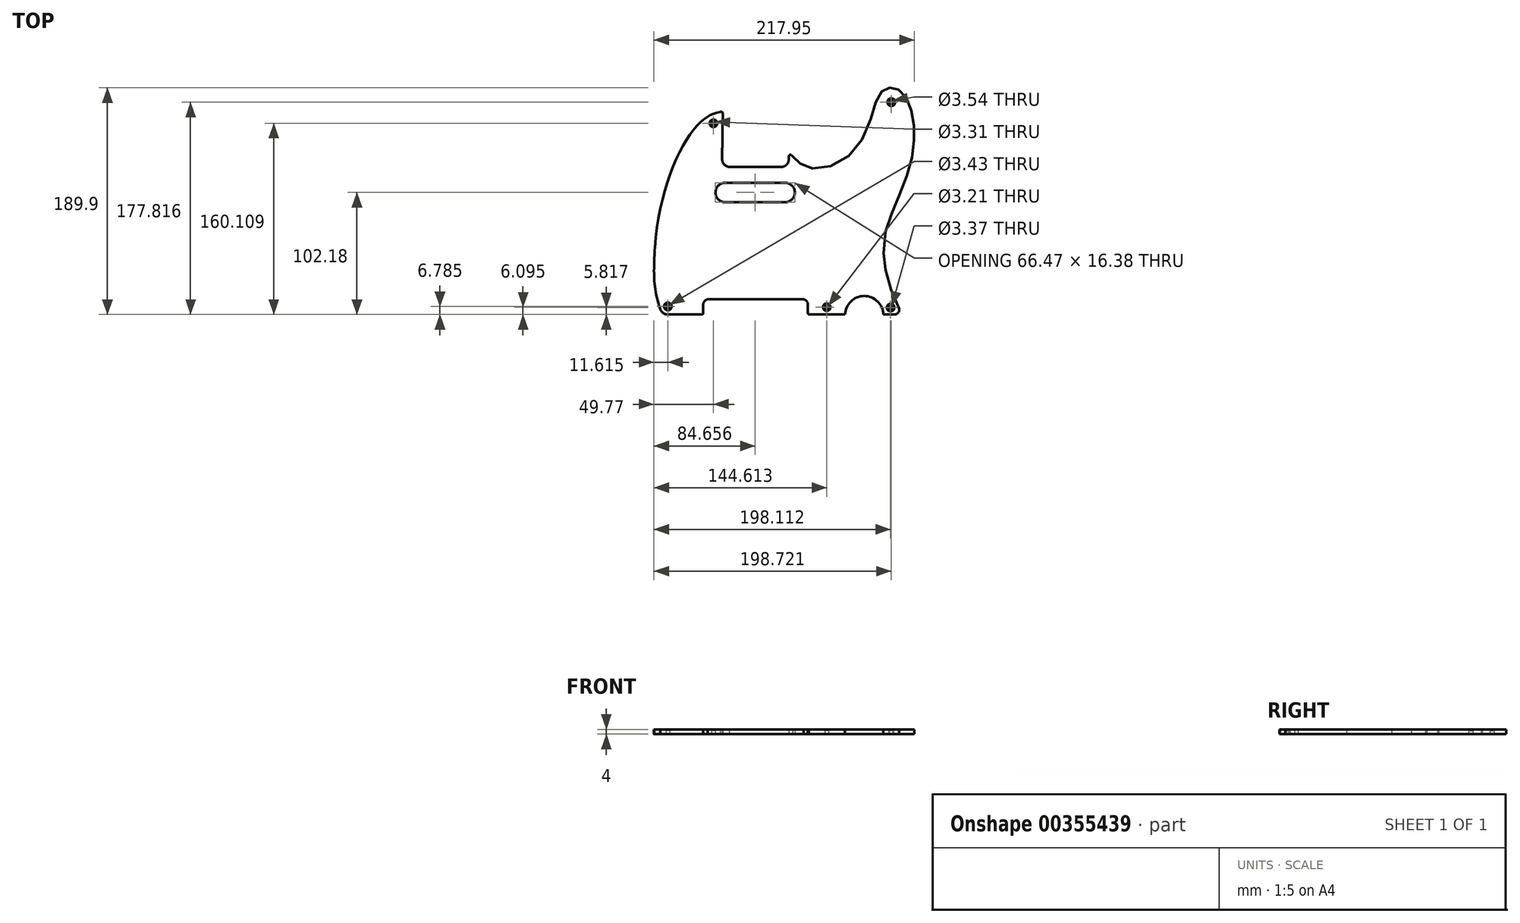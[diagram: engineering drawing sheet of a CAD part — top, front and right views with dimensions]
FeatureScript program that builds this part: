
annotation { "Feature Type Name" : "Feature", "Feature Type Description" : "" }
export const myFeature = defineFeature(function(context is Context, id is Id, definition is map)
    precondition{}
    {
        {
            var Q0;
            Q0=qCreatedBy(makeId("Top.planeOp"),FACE);
            var sketch = newSketch(context, id + "F0", { "sketchPlane" : qUnion([Q0])});
            skPoint(sketch, "E0.middle", {"position": v(0, 0) * mm});
            skCircle(sketch, "E1", {"center": v(-19.35, 182.39) * mm, "radius": 1.77 * mm});
            skCircle(sketch, "E2", {"center": v(-168.3, 164.68) * mm, "radius": 1.66 * mm});
            skLineSegment(sketch, "E3", {"start": v(-168.3, 164.68) * mm, "end": v(-19.35, 182.39) * mm, "construction": true});
            skCircle(sketch, "E4", {"center": v(-206.45, 11.36) * mm, "radius": 1.71 * mm});
            skCircle(sketch, "E5", {"center": v(-73.46, 10.66) * mm, "radius": 1.6 * mm});
            skCircle(sketch, "E6", {"center": v(-19.96, 10.39) * mm, "radius": 1.69 * mm});
            skLineSegment(sketch, "E7", {"start": v(-168.3, 164.68) * mm, "end": v(-206.45, 11.36) * mm, "construction": true});
            skLineSegment(sketch, "E8", {"start": v(-19.35, 182.39) * mm, "end": v(-19.96, 10.39) * mm, "construction": true});
            skLineSegment(sketch, "E9", {"start": v(-206.45, 11.36) * mm, "end": v(-73.46, 10.66) * mm, "construction": true});
            skLineSegment(sketch, "E10", {"start": v(-73.46, 10.66) * mm, "end": v(-19.96, 10.39) * mm, "construction": true});
            skLineSegment(sketch, "E11", {"start": v(-178.02, 4.57) * mm, "end": v(-206.45, 4.57) * mm});
            skArc(sketch, "E12", {"start": v(-206.45, 4.57) * mm, "mid": v(-210.44, 5.86) * mm, "end": v(-212.9, 9.25) * mm});
            skArc(sketch, "E13", {"start": v(-178.02, 4.57) * mm, "mid": v(-177.3, 4.81) * mm, "end": v(-176.88, 5.45) * mm});
            skLineSegment(sketch, "E14", {"start": v(-176.88, 5.45) * mm, "end": v(-176.88, 13.3) * mm});
            skArc(sketch, "E15", {"start": v(-173.21, 17.36) * mm, "mid": v(-175.63, 15.86) * mm, "end": v(-176.88, 13.3) * mm});
            skLineSegment(sketch, "E16", {"start": v(-173.21, 17.36) * mm, "end": v(-92.81, 17.36) * mm});
            skArc(sketch, "E17", {"start": v(-89.24, 13.4) * mm, "mid": v(-90.42, 15.92) * mm, "end": v(-92.81, 17.36) * mm});
            skLineSegment(sketch, "E18", {"start": v(-89.24, 13.4) * mm, "end": v(-89.24, 5.9) * mm});
            skArc(sketch, "E19", {"start": v(-89.24, 5.9) * mm, "mid": v(-89.04, 5.13) * mm, "end": v(-88.49, 4.57) * mm});
            skLineSegment(sketch, "E20", {"start": v(-88.49, 4.57) * mm, "end": v(-58.05, 4.57) * mm});
            skArc(sketch, "E21", {"start": v(-26.02, 4.57) * mm, "mid": v(-42.04, 20.07) * mm, "end": v(-58.05, 4.57) * mm});
            skLineSegment(sketch, "E22", {"start": v(-133.01, 17.36) * mm, "end": v(-133.01, -7.61) * mm});
            skLineSegment(sketch, "E23", {"start": v(-26.02, 4.57) * mm, "end": v(-16.76, 4.57) * mm});
            skArc(sketch, "E24", {"start": v(-16.76, 4.57) * mm, "mid": v(-13.6, 6.12) * mm, "end": v(-12.86, 9.57) * mm});
            skFitSpline(sketch, "E25", {"points": [v(-212.9, 9.25) * mm, v(-217.39, 60.66) * mm], "startDerivative": vector(-20.15, 57.1) * mm, "endDerivative": vector(2.26, 50.09) * mm});
            skFitSpline(sketch, "E26", {"points": [v(-217.39, 60.66) * mm, v(-183.96, 160.65) * mm, v(-162.78, 174.32) * mm], "startDerivative": vector(12.5, 194.87) * mm, "endDerivative": vector(62.55, 11.21) * mm});
            skLineSegment(sketch, "E27", {"start": v(-160.97, 134.38) * mm, "end": v(-160.56, 173.36) * mm});
            skFitSpline(sketch, "E28", {"points": [v(-162.78, 174.32) * mm, v(-161.45, 174.32) * mm, v(-160.56, 173.36) * mm], "startDerivative": vector(3.21, 0.26) * mm, "endDerivative": vector(1.04, -3.83) * mm});
            skArc(sketch, "E29", {"start": v(-160.97, 134.38) * mm, "mid": v(-159.24, 130.04) * mm, "end": v(-154.96, 128.16) * mm});
            skLineSegment(sketch, "E30", {"start": v(-154.96, 128.16) * mm, "end": v(-111.44, 128.16) * mm});
            skArc(sketch, "E31", {"start": v(-111.44, 128.16) * mm, "mid": v(-107.05, 129.99) * mm, "end": v(-105.26, 134.39) * mm});
            skLineSegment(sketch, "E32", {"start": v(-105.26, 137.04) * mm, "end": v(-105.26, 134.39) * mm});
            skFitSpline(sketch, "E33", {"points": [v(-105.26, 137.04) * mm, v(-101.96, 137.04) * mm], "startDerivative": vector(2.71, 7.99) * mm, "endDerivative": vector(1.53, -1.27) * mm});
            skFitSpline(sketch, "E34", {"points": [v(-12.86, 9.57) * mm, v(-17.7, 20.66) * mm, v(-22.68, 34.34) * mm, v(-24.82, 45.89) * mm, v(-25.82, 53.58) * mm, v(-25.08, 68.74) * mm, v(-22.74, 78.57) * mm, v(-18.85, 89.83) * mm, v(-13.4, 102.83) * mm, v(-8.78, 114.1) * mm, v(-4.77, 126.02) * mm, v(-2.07, 136.39) * mm, v(-0.63, 145.86) * mm, v(-0.12, 154.77) * mm, v(-0.37, 161.1) * mm, v(-1.1, 167.45) * mm, v(-2.5, 174.97) * mm, v(-3.72, 179.13) * mm, v(-6.29, 185.18) * mm, v(-9.27, 189.76) * mm, v(-11.97, 192.2) * mm, v(-15.18, 193.85) * mm, v(-17.8, 194.42) * mm, v(-19.67, 194.44) * mm, v(-22.19, 194.2) * mm, v(-23.88, 193.67) * mm, v(-26.53, 192.2) * mm, v(-28.77, 190) * mm, v(-31.45, 185.15) * mm, v(-33.5, 179.12) * mm, v(-36.18, 169.42) * mm, v(-41.23, 155.86) * mm, v(-49.68, 142.68) * mm, v(-58.8, 134.52) * mm, v(-71.85, 128.33) * mm, v(-82.35, 126.82) * mm, v(-89.76, 127.87) * mm, v(-94.34, 129.9) * mm, v(-97.85, 132.58) * mm, v(-100.24, 134.95) * mm, v(-101.96, 137.04) * mm, v(-102.75, 137.74) * mm], "startDerivative": vector(-150.29, 340.6) * mm, "endDerivative": vector(-84.46, 63.08) * mm});
            skLineSegment(sketch, "E35.bottom", {"start": v(-158.46, 98.56) * mm, "end": v(-108.37, 98.56) * mm});
            skLineSegment(sketch, "E35.top", {"start": v(-158.46, 114.94) * mm, "end": v(-108.37, 114.94) * mm});
            skLineSegment(sketch, "E35.left", {"start": v(-166.65, 106.75) * mm, "end": v(-166.65, 106.75) * mm});
            skLineSegment(sketch, "E35.right", {"start": v(-100.18, 106.75) * mm, "end": v(-100.18, 106.75) * mm});
            skPoint(sketch, "E36.visualSharp", {"position": v(-166.65, 114.94) * mm});
            skArc(sketch, "E36.filletArc", {"start": v(-158.46, 114.94) * mm, "mid": v(-164.25, 112.54) * mm, "end": v(-166.65, 106.75) * mm});
            skPoint(sketch, "E37.visualSharp", {"position": v(-166.65, 98.56) * mm});
            skArc(sketch, "E37.filletArc", {"start": v(-166.65, 106.75) * mm, "mid": v(-164.25, 100.96) * mm, "end": v(-158.46, 98.56) * mm});
            skPoint(sketch, "E38.visualSharp", {"position": v(-100.18, 114.94) * mm});
            skArc(sketch, "E38.filletArc", {"start": v(-100.18, 106.75) * mm, "mid": v(-102.58, 112.54) * mm, "end": v(-108.37, 114.94) * mm});
            skPoint(sketch, "E39.visualSharp", {"position": v(-100.18, 98.56) * mm});
            skArc(sketch, "E39.filletArc", {"start": v(-108.37, 98.56) * mm, "mid": v(-102.58, 100.96) * mm, "end": v(-100.18, 106.75) * mm});
            skSolve(sketch);
        }
        {
            var Q0;
            Q0=makeQuery(id+"F0.imprint","IMPRINT",FACE,{"disambiguationData":[TD([[makeQuery(id+"F0.imprint","IMPRINT",EDGE,{"derivedFrom":sQuery(id+"F0.wireOp",EDGE,"E1")}),-1.0]])]});
            extrude(context, id + "F1", {"entities" : qUnion([Q0]), "depth" : 4 * mm, "offsetDistance" : 25 * mm});
        }
        {
            var Q0;
            Q0=makeQuery(id+"F1.opExtrude","CAP_EDGE",EDGE,{"disambiguationData":[OSD([sQuery(id+"F0.wireOp",EDGE,"E2")])],"isStart":false});
            var Q1;
            Q1=makeQuery(id+"F1.opExtrude","CAP_EDGE",EDGE,{"disambiguationData":[OSD([sQuery(id+"F0.wireOp",EDGE,"E1")])],"isStart":false});
            var Q2;
            Q2=makeQuery(id+"F1.opExtrude","CAP_EDGE",EDGE,{"disambiguationData":[OSD([sQuery(id+"F0.wireOp",EDGE,"E6")])],"isStart":false});
            var Q3;
            Q3=makeQuery(id+"F1.opExtrude","CAP_EDGE",EDGE,{"disambiguationData":[OSD([sQuery(id+"F0.wireOp",EDGE,"E5")])],"isStart":false});
            var Q4;
            Q4=makeQuery(id+"F1.opExtrude","CAP_EDGE",EDGE,{"disambiguationData":[OSD([sQuery(id+"F0.wireOp",EDGE,"E4")])],"isStart":false});
            chamfer(context, id + "F2", {"entities" : qUnion([Q0, Q1, Q2, Q3, Q4]), "chamferType" : ChamferType.TWO_OFFSETS, "width1" : 1 * mm, "oppositeDirection" : false, "width2" : 1.5 * mm, "tangentPropagation" : true});
        }
    });
